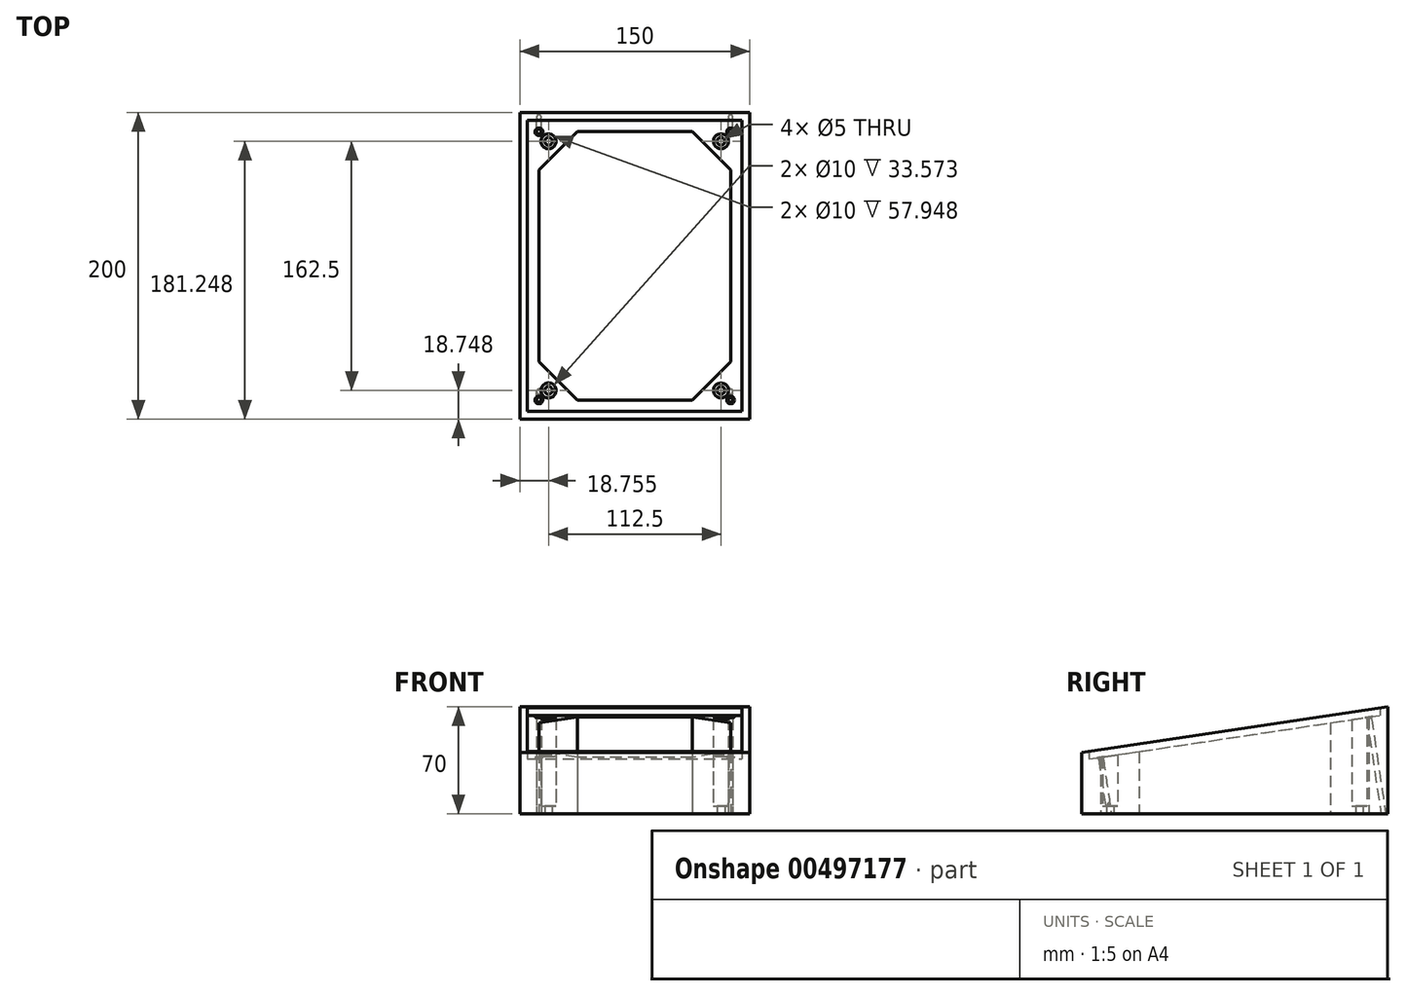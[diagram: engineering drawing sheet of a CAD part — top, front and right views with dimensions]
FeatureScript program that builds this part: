
annotation { "Feature Type Name" : "Feature", "Feature Type Description" : "" }
export const myFeature = defineFeature(function(context is Context, id is Id, definition is map)
    precondition{}
    {
        {
            var Q0;
            Q0=qCreatedBy(makeId("Top.planeOp"),FACE);
            var sketch = newSketch(context, id + "F0", { "sketchPlane" : qUnion([Q0])});
            skLineSegment(sketch, "E0.bottom", {"start": v(-75, 99.92) * mm, "end": v(75, 99.92) * mm});
            skLineSegment(sketch, "E0.top", {"start": v(-75, -100.08) * mm, "end": v(75, -100.08) * mm});
            skLineSegment(sketch, "E0.left", {"start": v(-75, 99.92) * mm, "end": v(-75, -100.08) * mm});
            skLineSegment(sketch, "E0.right", {"start": v(75, 99.92) * mm, "end": v(75, -100.08) * mm});
            skLineSegment(sketch, "E1.bottom", {"start": v(-68.75, 93.67) * mm, "end": v(68.75, 93.67) * mm});
            skLineSegment(sketch, "E1.top", {"start": v(-68.75, -93.83) * mm, "end": v(68.75, -93.83) * mm});
            skLineSegment(sketch, "E1.left", {"start": v(-68.75, 93.67) * mm, "end": v(-68.75, -93.83) * mm});
            skLineSegment(sketch, "E1.right", {"start": v(68.75, 93.67) * mm, "end": v(68.75, -93.83) * mm});
            skLineSegment(sketch, "E2.bottom", {"start": v(-62.5, 87.42) * mm, "end": v(62.5, 87.42) * mm});
            skLineSegment(sketch, "E2.top", {"start": v(-62.5, -87.58) * mm, "end": v(62.5, -87.58) * mm});
            skLineSegment(sketch, "E2.left", {"start": v(-62.5, 87.42) * mm, "end": v(-62.5, -87.58) * mm});
            skLineSegment(sketch, "E2.right", {"start": v(62.5, 87.42) * mm, "end": v(62.5, -87.58) * mm});
            skPoint(sketch, "E3", {"position": v(37.5, 87.42) * mm});
            skPoint(sketch, "E4", {"position": v(37.5, -87.58) * mm});
            skPoint(sketch, "E5", {"position": v(-37.5, 87.42) * mm});
            skPoint(sketch, "E6", {"position": v(-37.5, -87.58) * mm});
            skPoint(sketch, "E7", {"position": v(-62.5, 62.42) * mm});
            skPoint(sketch, "E8", {"position": v(62.5, 62.42) * mm});
            skPoint(sketch, "E9", {"position": v(62.5, -62.58) * mm});
            skPoint(sketch, "E10", {"position": v(-62.5, -62.58) * mm});
            skPoint(sketch, "E11", {"position": v(-62.5, 87.42) * mm});
            skPoint(sketch, "E12", {"position": v(62.5, 87.42) * mm});
            skPoint(sketch, "E13", {"position": v(62.5, -87.58) * mm});
            skPoint(sketch, "E14", {"position": v(-62.5, -87.58) * mm});
            skLineSegment(sketch, "E15", {"start": v(-62.5, -62.58) * mm, "end": v(-37.5, -87.58) * mm});
            skLineSegment(sketch, "E16", {"start": v(37.5, -87.58) * mm, "end": v(62.5, -62.58) * mm});
            skLineSegment(sketch, "E17", {"start": v(62.5, 62.42) * mm, "end": v(37.5, 87.42) * mm});
            skLineSegment(sketch, "E18", {"start": v(-37.5, 87.42) * mm, "end": v(-62.5, 62.42) * mm});
            skPoint(sketch, "E19", {"position": v(-50, 74.92) * mm});
            skPoint(sketch, "E20", {"position": v(50, 74.92) * mm});
            skPoint(sketch, "E21", {"position": v(50, -75.08) * mm});
            skPoint(sketch, "E22", {"position": v(-50, -75.08) * mm});
            skLineSegment(sketch, "E23", {"start": v(-62.5, 87.42) * mm, "end": v(-50, 74.92) * mm, "construction": true});
            skLineSegment(sketch, "E24", {"start": v(62.5, 87.42) * mm, "end": v(50, 74.92) * mm, "construction": true});
            skLineSegment(sketch, "E25", {"start": v(62.5, -87.58) * mm, "end": v(50, -75.08) * mm, "construction": true});
            skLineSegment(sketch, "E26", {"start": v(-62.5, -87.58) * mm, "end": v(-50, -75.08) * mm, "construction": true});
            skPoint(sketch, "E27", {"position": v(-56.25, 81.17) * mm});
            skPoint(sketch, "E28", {"position": v(56.25, 81.17) * mm});
            skPoint(sketch, "E29", {"position": v(56.25, -81.33) * mm});
            skPoint(sketch, "E30", {"position": v(-56.25, -81.33) * mm});
            skCircle(sketch, "E31", {"center": v(-56.25, -81.33) * mm, "radius": 2.5 * mm});
            skCircle(sketch, "E32", {"center": v(56.25, -81.33) * mm, "radius": 2.5 * mm});
            skCircle(sketch, "E33", {"center": v(56.25, 81.17) * mm, "radius": 2.5 * mm});
            skCircle(sketch, "E34", {"center": v(-56.25, 81.17) * mm, "radius": 2.5 * mm});
            skCircle(sketch, "E35", {"center": v(-56.25, 81.17) * mm, "radius": 5 * mm});
            skCircle(sketch, "E36", {"center": v(56.25, 81.17) * mm, "radius": 5 * mm});
            skCircle(sketch, "E37", {"center": v(-56.25, -81.33) * mm, "radius": 5 * mm});
            skCircle(sketch, "E38", {"center": v(56.25, -81.33) * mm, "radius": 5 * mm});
            skSolve(sketch);
        }
        {
            var Q0;
            Q0=makeQuery(id+"F0.imprint","IMPRINT",FACE,{"disambiguationData":[TD([[makeQuery(id+"F0.imprint","IMPRINT",EDGE,{"derivedFrom":sQuery(id+"F0.wireOp",EDGE,"E0.bottom")}),-1.0]])]});
            var Q1;
            Q1=makeQuery(id+"F0.imprint","IMPRINT",FACE,{"disambiguationData":[TD([[makeQuery(id+"F0.imprint","IMPRINT",EDGE,{"derivedFrom":sQuery(id+"F0.wireOp",EDGE,"E1.bottom")}),-1.0]])]});
            var Q2;
            {var subQ5=sQuery(id+"F0.wireOp",EDGE,"E18");Q2=makeQuery(id+"F0.imprint","IMPRINT",FACE,{"disambiguationData":[TD([[makeQuery(id+"F0.imprint","IMPRINT",EDGE,{"derivedFrom":subQ5}),-1.0]])]});}
            var Q3;
            {var subQ0=sQuery(id+"F0.wireOp",EDGE,"E17");Q3=makeQuery(id+"F0.imprint","IMPRINT",FACE,{"disambiguationData":[TD([[makeQuery(id+"F0.imprint","IMPRINT",EDGE,{"derivedFrom":subQ0}),-1.0]])]});}
            var Q4;
            {var subQ0=sQuery(id+"F0.wireOp",EDGE,"E16");Q4=makeQuery(id+"F0.imprint","IMPRINT",FACE,{"disambiguationData":[TD([[makeQuery(id+"F0.imprint","IMPRINT",EDGE,{"derivedFrom":subQ0}),-1.0]])]});}
            var Q5;
            {var subQ5=sQuery(id+"F0.wireOp",EDGE,"E15");Q5=makeQuery(id+"F0.imprint","IMPRINT",FACE,{"disambiguationData":[TD([[makeQuery(id+"F0.imprint","IMPRINT",EDGE,{"derivedFrom":subQ5}),-1.0]])]});}
            extrude(context, id + "F1", {"entities" : qUnion([Q0, Q1, Q2, Q3, Q4, Q5]), "depth" : 70 * mm});
        }
        {
            var Q0;
            Q0=makeQuery(id+"F1.opExtrude","SWEPT_FACE",FACE,{"disambiguationData":[OSD([sQuery(id+"F0.wireOp",EDGE,"E0.right")])]});
            var sketch = newSketch(context, id + "F2", { "sketchPlane" : qUnion([Q0])});
            skPoint(sketch, "E39", {"position": v(-100.08, 40) * mm});
            skLineSegment(sketch, "E40", {"start": v(-100.08, 40) * mm, "end": v(99.92, 70) * mm});
            skLineSegment(sketch, "E41", {"start": v(-100.08, 70) * mm, "end": v(-100.08, 40) * mm});
            skLineSegment(sketch, "E42", {"start": v(-100.08, 70) * mm, "end": v(99.92, 70) * mm});
            skSolve(sketch);
        }
        {
            var Q0;
            Q0=makeQuery(id+"F2.imprint","IMPRINT",FACE,{"disambiguationData":[TD([[makeQuery(id+"F2.imprint","IMPRINT",EDGE,{"derivedFrom":sQuery(id+"F2.wireOp",EDGE,"E40")}),1.0]])]});
            extrude(context, id + "F3", {"entities" : qUnion([Q0]), "operationType" : NewBodyOperationType.REMOVE, "oppositeDirection" : true, "depth" : 155 * mm});
        }
        {
            var Q0;
            Q0=makeQuery(id+"F1.opExtrude","SWEPT_FACE",FACE,{"disambiguationData":[OSD([sQuery(id+"F0.wireOp",EDGE,"E0.right")])]});
            var sketch = newSketch(context, id + "F4", { "sketchPlane" : qUnion([Q0])});
            skPoint(sketch, "E43", {"position": v(94.92, 69.25) * mm});
            skPoint(sketch, "E44", {"position": v(-95.08, 40.75) * mm});
            skPoint(sketch, "E45", {"position": v(94.92, 64.25) * mm});
            skPoint(sketch, "E46", {"position": v(-95.08, 35.75) * mm});
            skLineSegment(sketch, "E47", {"start": v(-95.08, 40.75) * mm, "end": v(-95.08, 35.75) * mm});
            skLineSegment(sketch, "E48", {"start": v(-95.08, 35.75) * mm, "end": v(94.92, 64.25) * mm});
            skLineSegment(sketch, "E49", {"start": v(94.92, 64.25) * mm, "end": v(94.92, 69.25) * mm});
            skLineSegment(sketch, "E50", {"start": v(94.92, 69.25) * mm, "end": v(-95.08, 40.75) * mm});
            skSolve(sketch);
        }
        {
            var Q0;
            Q0=makeQuery(id+"F4.imprint","IMPRINT",FACE,{"disambiguationData":[TD([[makeQuery(id+"F4.imprint","IMPRINT",EDGE,{"derivedFrom":sQuery(id+"F4.wireOp",EDGE,"E47")}),1.0]])]});
            extrude(context, id + "F5", {"entities" : qUnion([Q0]), "operationType" : NewBodyOperationType.REMOVE, "oppositeDirection" : true, "depth" : 145 * mm, "hasSecondDirection" : true, "secondDirectionOppositeDirection" : true, "secondDirectionDepth" : 5 * mm});
        }
        {
            var Q0;
            Q0=makeQuery(id+"F0.imprint","IMPRINT",FACE,{"disambiguationData":[TD([[makeQuery(id+"F0.imprint","IMPRINT",EDGE,{"derivedFrom":sQuery(id+"F0.wireOp",EDGE,"E34")}),-1.0]])]});
            var Q1;
            Q1=makeQuery(id+"F0.imprint","IMPRINT",FACE,{"disambiguationData":[TD([[makeQuery(id+"F0.imprint","IMPRINT",EDGE,{"derivedFrom":sQuery(id+"F0.wireOp",EDGE,"E33")}),-1.0]])]});
            var Q2;
            Q2=makeQuery(id+"F0.imprint","IMPRINT",FACE,{"disambiguationData":[TD([[makeQuery(id+"F0.imprint","IMPRINT",EDGE,{"derivedFrom":sQuery(id+"F0.wireOp",EDGE,"E31")}),-1.0]])]});
            var Q3;
            Q3=makeQuery(id+"F0.imprint","IMPRINT",FACE,{"disambiguationData":[TD([[makeQuery(id+"F0.imprint","IMPRINT",EDGE,{"derivedFrom":sQuery(id+"F0.wireOp",EDGE,"E32")}),-1.0]])]});
            extrude(context, id + "F6", {"entities" : qUnion([Q0, Q1, Q2, Q3]), "operationType" : NewBodyOperationType.ADD, "depth" : 5 * mm});
        }
        {
            var Q0;
            Q0=makeQuery(id+"F5.boolean.opBoolean","COPY",FACE,{"derivedFrom":makeQuery(id+"F5.opExtrude","SWEPT_FACE",FACE,{"disambiguationData":[OSD([sQuery(id+"F4.wireOp",EDGE,"E48")])]})});
            var sketch = newSketch(context, id + "F7", { "sketchPlane" : qUnion([Q0])});
            skPoint(sketch, "E51", {"position": v(-62.5, 95.81) * mm});
            skPoint(sketch, "E52", {"position": v(62.5, 95.81) * mm});
            skPoint(sketch, "E53", {"position": v(62.5, -81.14) * mm});
            skPoint(sketch, "E54", {"position": v(-62.5, -81.14) * mm});
            skPoint(sketch, "E55", {"position": v(-70, -88.73) * mm});
            skPoint(sketch, "E56", {"position": v(70, -88.73) * mm});
            skPoint(sketch, "E57", {"position": v(-70, 103.4) * mm});
            skSolve(sketch);
        }
        {
            var Q0;
            Q0=sQuery(id+"F7.wireOp",VERTEX,"E51");
            var Q1;
            Q1=sQuery(id+"F7.wireOp",VERTEX,"E52");
            var Q2;
            Q2=sQuery(id+"F7.wireOp",VERTEX,"E53");
            var Q3;
            Q3=sQuery(id+"F7.wireOp",VERTEX,"E54");
            var Q4;
            Q4=makeQuery(id+"F1.opExtrude","SWEPT_BODY",BODY,{"disambiguationData":[OSD([sQuery(id+"F0.wireOp",EDGE,"E0.bottom"),sQuery(id+"F0.wireOp",EDGE,"E0.top"),sQuery(id+"F0.wireOp",EDGE,"E0.left"),sQuery(id+"F0.wireOp",EDGE,"E0.right"),sQuery(id+"F0.wireOp",EDGE,"E2.bottom"),sQuery(id+"F0.wireOp",EDGE,"E2.top"),sQuery(id+"F0.wireOp",EDGE,"E2.left"),sQuery(id+"F0.wireOp",EDGE,"E2.right"),sQuery(id+"F0.wireOp",EDGE,"E15"),sQuery(id+"F0.wireOp",EDGE,"E16"),sQuery(id+"F0.wireOp",EDGE,"E17"),sQuery(id+"F0.wireOp",EDGE,"E18"),sQuery(id+"F0.wireOp",EDGE,"E35"),sQuery(id+"F0.wireOp",EDGE,"E36"),sQuery(id+"F0.wireOp",EDGE,"E37"),sQuery(id+"F0.wireOp",EDGE,"E38")])]});
            hole(context, id + "F8", {"style" : HoleStyle.C_SINK, "endStyle" : HoleEndStyle.THROUGH, "holeDiameter" : 3 * mm, "cSinkDiameter" : 5 * mm, "cSinkAngle" : 90 * degree, "isTappedThrough" : true, "tappedDepth" : 12 * mm, "tapClearance" : 3, "locations" : qUnion([Q0, Q1, Q2, Q3]), "scope" : qUnion([Q4])});
        }
    });
